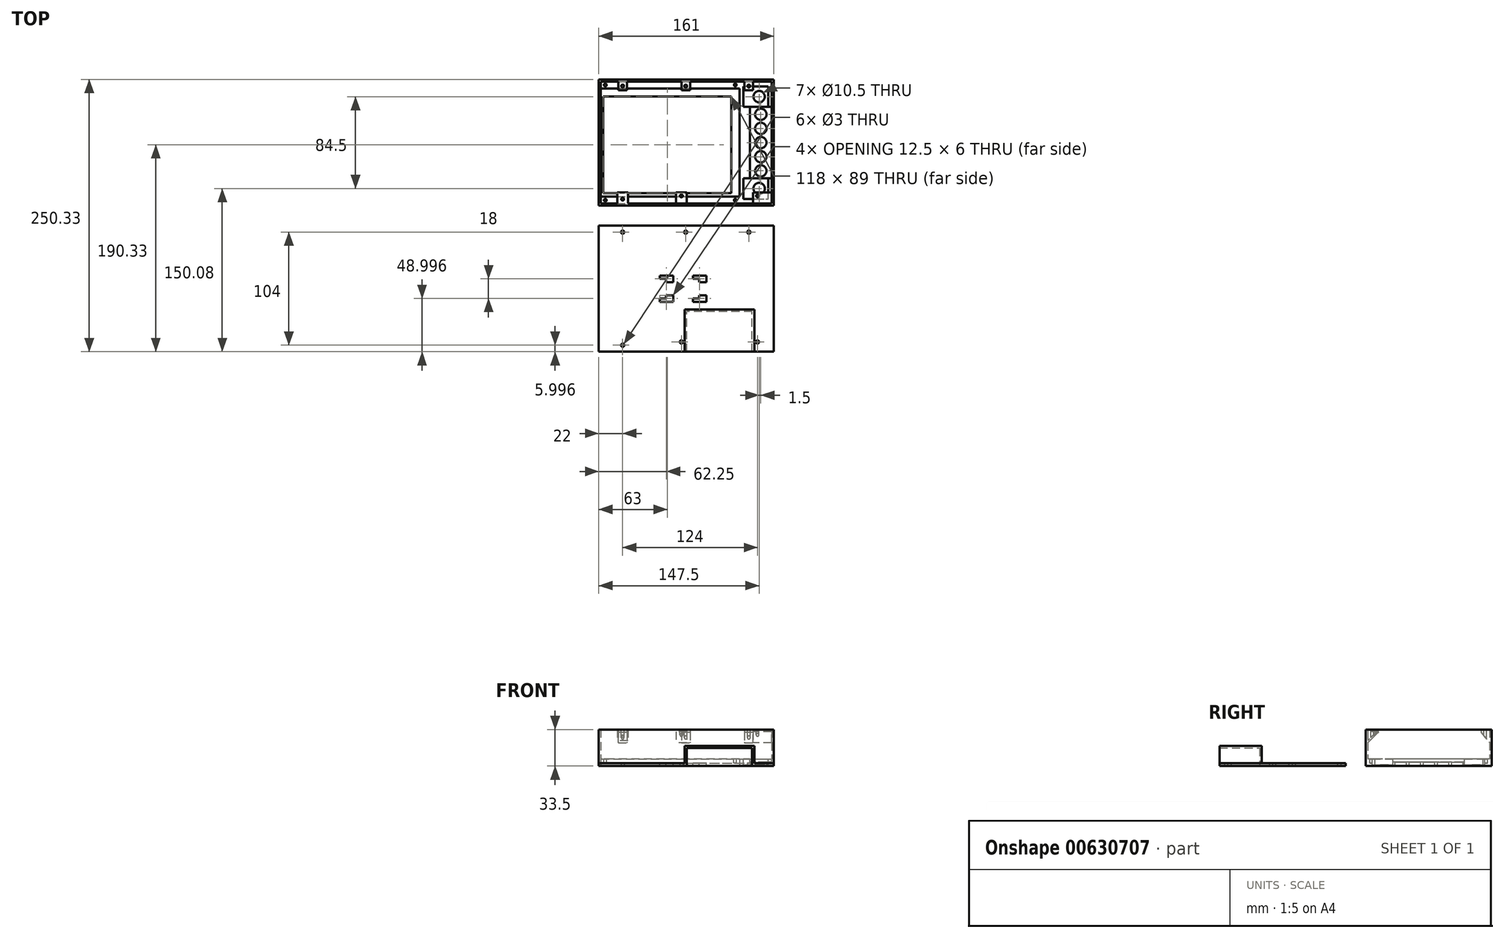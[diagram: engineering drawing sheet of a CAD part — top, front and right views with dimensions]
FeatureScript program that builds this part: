
annotation { "Feature Type Name" : "Feature", "Feature Type Description" : "" }
export const myFeature = defineFeature(function(context is Context, id is Id, definition is map)
    precondition{}
    {
        {
            var Q0;
            Q0=qCreatedBy(makeId("Top.planeOp"),FACE);
            var sketch = newSketch(context, id + "F0", { "sketchPlane" : qUnion([Q0])});
            skLineSegment(sketch, "E0.bottom", {"start": v(58, -44.5) * mm, "end": v(-60, -44.5) * mm});
            skLineSegment(sketch, "E0.top", {"start": v(58, 44.5) * mm, "end": v(-60, 44.5) * mm});
            skLineSegment(sketch, "E0.left", {"start": v(58, -44.5) * mm, "end": v(58, 44.5) * mm});
            skLineSegment(sketch, "E0.right", {"start": v(-60, -44.5) * mm, "end": v(-60, 44.5) * mm});
            skPoint(sketch, "E0.middle", {"position": v(0, 0) * mm});
            skLineSegment(sketch, "E1", {"start": v(65.5, 51.75) * mm, "end": v(-62, 51.75) * mm});
            skLineSegment(sketch, "E2", {"start": v(-62, 51.75) * mm, "end": v(-62, -47.75) * mm});
            skLineSegment(sketch, "E3", {"start": v(-62, -47.75) * mm, "end": v(65.5, -47.75) * mm});
            skLineSegment(sketch, "E4", {"start": v(97, 60) * mm, "end": v(97, -56) * mm});
            skLineSegment(sketch, "E5", {"start": v(65.5, 51.75) * mm, "end": v(65.5, -47.75) * mm});
            skLineSegment(sketch, "E6", {"start": v(97, 60) * mm, "end": v(-64, 60) * mm});
            skLineSegment(sketch, "E7", {"start": v(-64, 60) * mm, "end": v(-64, -56) * mm});
            skLineSegment(sketch, "E8", {"start": v(-64, -56) * mm, "end": v(97, -56) * mm});
            skLineSegment(sketch, "E9", {"start": v(-113.4, 0) * mm, "end": v(104.3, 0) * mm, "construction": true});
            skLineSegment(sketch, "E10", {"start": v(0, 75.63) * mm, "end": v(0, -66.3) * mm, "construction": true});
            skSolve(sketch);
        }
        {
            var Q0;
            Q0=makeQuery(id+"F0.imprint","IMPRINT",FACE,{"disambiguationData":[TD([[makeQuery(id+"F0.imprint","IMPRINT",EDGE,{"derivedFrom":sQuery(id+"F0.wireOp",EDGE,"E1")}),-1.0]])]});
            var sketch = newSketch(context, id + "F1", { "sketchPlane" : qUnion([Q0])});
            skLineSegment(sketch, "E11", {"start": v(-84.5, 2) * mm, "end": v(108.61, 2) * mm, "construction": true});
            skCircle(sketch, "E12", {"center": v(83.5, -40.25) * mm, "radius": 5.25 * mm});
            skCircle(sketch, "E13", {"center": v(83.5, 44.25) * mm, "radius": 5.25 * mm});
            skCircle(sketch, "E14", {"center": v(85, -24) * mm, "radius": 5.25 * mm});
            skCircle(sketch, "E15", {"center": v(85, -11) * mm, "radius": 5.25 * mm});
            skCircle(sketch, "E16", {"center": v(85, 2) * mm, "radius": 5.25 * mm});
            skCircle(sketch, "E17", {"center": v(85, 15) * mm, "radius": 5.25 * mm});
            skCircle(sketch, "E18", {"center": v(85, 28) * mm, "radius": 5.25 * mm});
            skLineSegment(sketch, "E19", {"start": v(83.5, -71.08) * mm, "end": v(83.5, 74.69) * mm, "construction": true});
            skLineSegment(sketch, "E20", {"start": v(85, -66.88) * mm, "end": v(85, 79.26) * mm, "construction": true});
            skLineSegment(sketch, "E21.0", {"start": v(97, 60) * mm, "end": v(-64, 60) * mm});
            skLineSegment(sketch, "E22.0", {"start": v(-64, -56) * mm, "end": v(97, -56) * mm});
            skSolve(sketch);
        }
        {
            var Q0;
            Q0=makeQuery(id+"F0.imprint","IMPRINT",FACE,{"disambiguationData":[TD([[makeQuery(id+"F0.imprint","IMPRINT",EDGE,{"derivedFrom":sQuery(id+"F0.wireOp",EDGE,"E1")}),-1.0]])]});
            extrude(context, id + "F2", {"entities" : qUnion([Q0]), "depth" : 6.5 * mm, "offsetDistance" : 25 * mm});
        }
        {
            var Q0;
            Q0=makeQuery(id+"F0.imprint","IMPRINT",FACE,{"disambiguationData":[TD([[makeQuery(id+"F0.imprint","IMPRINT",EDGE,{"derivedFrom":sQuery(id+"F0.wireOp",EDGE,"E0.bottom")}),1.0]])]});
            extrude(context, id + "F3", {"entities" : qUnion([Q0]), "operationType" : NewBodyOperationType.ADD, "depth" : 0.5 * mm, "offsetDistance" : 25 * mm});
        }
        {
            var Q0;
            Q0=qSketchRegion(id+"F1",true);
            extrude(context, id + "F4", {"entities" : qUnion([Q0]), "operationType" : NewBodyOperationType.REMOVE, "endBound" : BoundingType.UP_TO_NEXT, "depth" : 25 * mm, "offsetDistance" : 25 * mm});
        }
        {
            var Q0;
            Q0=makeQuery(id+"F2.opExtrude","CAP_FACE",FACE,{"disambiguationData":[OSD([sQuery(id+"F0.wireOp",EDGE,"E1"),sQuery(id+"F0.wireOp",EDGE,"E2"),sQuery(id+"F0.wireOp",EDGE,"E3"),sQuery(id+"F0.wireOp",EDGE,"uJP7YDUN-rWva-qcYO-6x3W-ZzMSHt70PE38"),sQuery(id+"F0.wireOp",EDGE,"E4"),sQuery(id+"F0.wireOp",EDGE,"uUVwlqNG-qbxU-A1Om-LvLD-7nAPouQdWURQ"),sQuery(id+"F0.wireOp",EDGE,"E5"),sQuery(id+"F0.wireOp",EDGE,"4ictx77T-zoG0-GI4i-ma4k-AJqkk2AVgenD"),sQuery(id+"F0.wireOp",EDGE,"E6"),sQuery(id+"F0.wireOp",EDGE,"E7"),sQuery(id+"F0.wireOp",EDGE,"E8"),sQuery(id+"F0.wireOp",EDGE,"cszChe2j-AEUY-pRS6-OkYU-3u1da41BygmN")])],"isStart":false});
            var sketch = newSketch(context, id + "F5", { "sketchPlane" : qUnion([Q0])});
            skLineSegment(sketch, "E23.bottom", {"start": v(92, 34.75) * mm, "end": v(75, 34.75) * mm});
            skLineSegment(sketch, "E23.top", {"start": v(92, 53.75) * mm, "end": v(75, 53.75) * mm});
            skLineSegment(sketch, "E23.left", {"start": v(92, 34.75) * mm, "end": v(92, 53.75) * mm});
            skLineSegment(sketch, "E23.right", {"start": v(75, 34.75) * mm, "end": v(75, 53.75) * mm});
            skPoint(sketch, "E23.middle", {"position": v(83.5, 44.25) * mm});
            skLineSegment(sketch, "E24", {"start": v(75, 53.75) * mm, "end": v(69, 53.75) * mm});
            skLineSegment(sketch, "E25", {"start": v(69, 53.75) * mm, "end": v(69, 34.75) * mm});
            skLineSegment(sketch, "E26", {"start": v(69, 34.75) * mm, "end": v(75, 34.75) * mm});
            skLineSegment(sketch, "E27.bottom", {"start": v(92, -49.75) * mm, "end": v(75, -49.75) * mm});
            skLineSegment(sketch, "E27.top", {"start": v(92, -30.75) * mm, "end": v(75, -30.75) * mm});
            skLineSegment(sketch, "E27.left", {"start": v(92, -49.75) * mm, "end": v(92, -30.75) * mm});
            skLineSegment(sketch, "E27.right", {"start": v(75, -49.75) * mm, "end": v(75, -30.75) * mm});
            skPoint(sketch, "E27.middle", {"position": v(83.5, -40.25) * mm});
            skLineSegment(sketch, "E28", {"start": v(75, -30.75) * mm, "end": v(69, -30.75) * mm});
            skLineSegment(sketch, "E29", {"start": v(69, -30.75) * mm, "end": v(69, -49.75) * mm});
            skLineSegment(sketch, "E30", {"start": v(69, -49.75) * mm, "end": v(75, -49.75) * mm});
            skLineSegment(sketch, "E31", {"start": v(75, 34.75) * mm, "end": v(75, -30.75) * mm});
            skLineSegment(sketch, "E32", {"start": v(92, 34.75) * mm, "end": v(95, 34.75) * mm});
            skLineSegment(sketch, "E33", {"start": v(95, 34.75) * mm, "end": v(95, -30.75) * mm});
            skLineSegment(sketch, "E34", {"start": v(95, -30.75) * mm, "end": v(92, -30.75) * mm});
            skSolve(sketch);
        }
        {
            var Q0;
            Q0=makeQuery(id+"F5.imprint","IMPRINT",FACE,{"disambiguationData":[TD([[makeQuery(id+"F5.imprint","IMPRINT",EDGE,{"derivedFrom":sQuery(id+"F5.wireOp",EDGE,"E23.right")}),1.0]])]});
            var Q1;
            Q1=makeQuery(id+"F5.imprint","IMPRINT",FACE,{"disambiguationData":[TD([[makeQuery(id+"F5.imprint","IMPRINT",EDGE,{"derivedFrom":sQuery(id+"F5.wireOp",EDGE,"E23.bottom")}),-1.0]])]});
            var Q2;
            Q2=makeQuery(id+"F5.imprint","IMPRINT",FACE,{"disambiguationData":[TD([[makeQuery(id+"F5.imprint","IMPRINT",EDGE,{"derivedFrom":sQuery(id+"F5.wireOp",EDGE,"E27.right")}),1.0]])]});
            var Q3;
            Q3=makeQuery(id+"F5.imprint","IMPRINT",FACE,{"disambiguationData":[TD([[makeQuery(id+"F5.imprint","IMPRINT",EDGE,{"derivedFrom":sQuery(id+"F5.wireOp",EDGE,"E27.bottom")}),-1.0]])]});
            extrude(context, id + "F6", {"entities" : qUnion([Q0, Q1, Q2, Q3]), "operationType" : NewBodyOperationType.REMOVE, "oppositeDirection" : true, "depth" : 5.5 * mm, "offsetDistance" : 25 * mm});
        }
        {
            var Q0;
            Q0=makeQuery(id+"F2.opExtrude","CAP_FACE",FACE,{"disambiguationData":[OSD([sQuery(id+"F0.wireOp",EDGE,"E1"),sQuery(id+"F0.wireOp",EDGE,"E2"),sQuery(id+"F0.wireOp",EDGE,"E3"),sQuery(id+"F0.wireOp",EDGE,"E4"),sQuery(id+"F0.wireOp",EDGE,"E5"),sQuery(id+"F0.wireOp",EDGE,"E6"),sQuery(id+"F0.wireOp",EDGE,"E7"),sQuery(id+"F0.wireOp",EDGE,"E8")])],"isStart":false});
            var sketch = newSketch(context, id + "F7", { "sketchPlane" : qUnion([Q0])});
            skLineSegment(sketch, "E35.bottom", {"start": v(-62, 58) * mm, "end": v(95, 58) * mm});
            skLineSegment(sketch, "E35.top", {"start": v(-62, -54) * mm, "end": v(95, -54) * mm});
            skLineSegment(sketch, "E35.left", {"start": v(-62, 58) * mm, "end": v(-62, -54) * mm});
            skLineSegment(sketch, "E35.right", {"start": v(95, 58) * mm, "end": v(95, -54) * mm});
            skSolve(sketch);
        }
        {
            var Q0;
            {var subQ2=sQuery(id+"F7.wireOp",EDGE,"E35.bottom");Q0=makeQuery(id+"F7.imprint","IMPRINT",FACE,{"disambiguationData":[TD([[makeQuery(id+"F7.imprint","IMPRINT",EDGE,{"derivedFrom":subQ2}),1.0]])]});}
            extrude(context, id + "F8", {"entities" : qUnion([Q0]), "operationType" : NewBodyOperationType.ADD, "depth" : 27 * mm, "offsetDistance" : 25 * mm});
        }
        {
            var Q0;
            Q0=makeQuery(id+"F2.opExtrude","CAP_FACE",FACE,{"disambiguationData":[OSD([sQuery(id+"F0.wireOp",EDGE,"E1"),sQuery(id+"F0.wireOp",EDGE,"E2"),sQuery(id+"F0.wireOp",EDGE,"E3"),sQuery(id+"F0.wireOp",EDGE,"E4"),sQuery(id+"F0.wireOp",EDGE,"E5"),sQuery(id+"F0.wireOp",EDGE,"E6"),sQuery(id+"F0.wireOp",EDGE,"E7"),sQuery(id+"F0.wireOp",EDGE,"E8")])],"isStart":false});
            var sketch = newSketch(context, id + "F9", { "sketchPlane" : qUnion([Q0])});
            skCircle(sketch, "E36", {"center": v(-58, 55) * mm, "radius": 1.25 * mm});
            skCircle(sketch, "E37", {"center": v(61.5, 55) * mm, "radius": 1.25 * mm});
            skCircle(sketch, "E38", {"center": v(61.5, -51) * mm, "radius": 1.25 * mm});
            skCircle(sketch, "E39", {"center": v(-58, -51) * mm, "radius": 1.25 * mm});
            skLineSegment(sketch, "E40", {"start": v(-58, 67) * mm, "end": v(-58, -65.08) * mm, "construction": true});
            skLineSegment(sketch, "E41", {"start": v(61.5, -67.24) * mm, "end": v(61.5, 67.67) * mm, "construction": true});
            skLineSegment(sketch, "E42", {"start": v(-91.1, 55) * mm, "end": v(105.33, 55) * mm, "construction": true});
            skLineSegment(sketch, "E43", {"start": v(-89.47, -51) * mm, "end": v(106.68, -51) * mm, "construction": true});
            skSolve(sketch);
        }
        {
            var Q0;
            Q0=makeQuery(id+"F9.imprint","IMPRINT",FACE,{"disambiguationData":[TD([[makeQuery(id+"F9.imprint","IMPRINT",EDGE,{"derivedFrom":sQuery(id+"F9.wireOp",EDGE,"E36")}),1.0]])]});
            var Q1;
            Q1=makeQuery(id+"F9.imprint","IMPRINT",FACE,{"disambiguationData":[TD([[makeQuery(id+"F9.imprint","IMPRINT",EDGE,{"derivedFrom":sQuery(id+"F9.wireOp",EDGE,"E37")}),1.0]])]});
            var Q2;
            Q2=makeQuery(id+"F9.imprint","IMPRINT",FACE,{"disambiguationData":[TD([[makeQuery(id+"F9.imprint","IMPRINT",EDGE,{"derivedFrom":sQuery(id+"F9.wireOp",EDGE,"E38")}),1.0]])]});
            var Q3;
            Q3=makeQuery(id+"F9.imprint","IMPRINT",FACE,{"disambiguationData":[TD([[makeQuery(id+"F9.imprint","IMPRINT",EDGE,{"derivedFrom":sQuery(id+"F9.wireOp",EDGE,"E39")}),1.0]])]});
            extrude(context, id + "F10", {"entities" : qUnion([Q0, Q1, Q2, Q3]), "operationType" : NewBodyOperationType.REMOVE, "oppositeDirection" : true, "depth" : 4 * mm, "offsetDistance" : 25 * mm});
        }
        {
            var Q0;
            Q0=makeQuery(id+"F8.opExtrude","SWEPT_FACE",FACE,{"disambiguationData":[OSD([sQuery(id+"F7.wireOp",EDGE,"E35.bottom")])]});
            var sketch = newSketch(context, id + "F11", { "sketchPlane" : qUnion([Q0])});
            skLineSegment(sketch, "E44.bottom", {"start": v(-46, 33.5) * mm, "end": v(-38, 33.5) * mm});
            skLineSegment(sketch, "E44.top", {"start": v(-46, 21.5) * mm, "end": v(-38, 21.5) * mm});
            skLineSegment(sketch, "E44.left", {"start": v(-46, 33.5) * mm, "end": v(-46, 21.5) * mm});
            skLineSegment(sketch, "E44.right", {"start": v(-38, 33.5) * mm, "end": v(-38, 21.5) * mm});
            skLineSegment(sketch, "E45.bottom", {"start": v(12, 33.5) * mm, "end": v(20, 33.5) * mm});
            skLineSegment(sketch, "E45.top", {"start": v(12, 21.5) * mm, "end": v(20, 21.5) * mm});
            skLineSegment(sketch, "E45.left", {"start": v(12, 33.5) * mm, "end": v(12, 21.5) * mm});
            skLineSegment(sketch, "E45.right", {"start": v(20, 33.5) * mm, "end": v(20, 21.5) * mm});
            skLineSegment(sketch, "E46.bottom", {"start": v(70, 33.5) * mm, "end": v(78, 33.5) * mm});
            skLineSegment(sketch, "E46.top", {"start": v(70, 21.5) * mm, "end": v(78, 21.5) * mm});
            skLineSegment(sketch, "E46.left", {"start": v(70, 33.5) * mm, "end": v(70, 21.5) * mm});
            skLineSegment(sketch, "E46.right", {"start": v(78, 33.5) * mm, "end": v(78, 21.5) * mm});
            skSolve(sketch);
        }
        {
            var Q0;
            Q0=makeQuery(id+"F11.imprint","IMPRINT",FACE,{"disambiguationData":[TD([[makeQuery(id+"F11.imprint","IMPRINT",EDGE,{"derivedFrom":sQuery(id+"F11.wireOp",EDGE,"E44.bottom")}),-1.0]])]});
            var Q1;
            Q1=makeQuery(id+"F11.imprint","IMPRINT",FACE,{"disambiguationData":[TD([[makeQuery(id+"F11.imprint","IMPRINT",EDGE,{"derivedFrom":sQuery(id+"F11.wireOp",EDGE,"E45.bottom")}),-1.0]])]});
            var Q2;
            Q2=makeQuery(id+"F11.imprint","IMPRINT",FACE,{"disambiguationData":[TD([[makeQuery(id+"F11.imprint","IMPRINT",EDGE,{"derivedFrom":sQuery(id+"F11.wireOp",EDGE,"E46.bottom")}),-1.0]])]});
            extrude(context, id + "F12", {"entities" : qUnion([Q0, Q1, Q2]), "operationType" : NewBodyOperationType.ADD, "depth" : 8 * mm, "offsetDistance" : 25 * mm});
        }
        {
            var Q0;
            Q0=makeQuery(id+"F12.opExtrude","SWEPT_FACE",FACE,{"disambiguationData":[OSD([sQuery(id+"F11.wireOp",EDGE,"E44.left")])]});
            var sketch = newSketch(context, id + "F13", { "sketchPlane" : qUnion([Q0])});
            skLineSegment(sketch, "E47", {"start": v(-58, 21.5) * mm, "end": v(-50, 31.03) * mm});
            skSolve(sketch);
        }
        {
            var Q0;
            {var subQ0=sQuery(id+"F13.wireOp",EDGE,"E47");Q0=makeQuery(id+"F13.imprint","IMPRINT",FACE,{"disambiguationData":[TD([[makeQuery(id+"F13.imprint","IMPRINT",EDGE,{"derivedFrom":subQ0}),-1.0]])]});}
            var Q1;
            Q1=makeQuery(id+"F12.opExtrude","SWEPT_FACE",FACE,{"disambiguationData":[OSD([sQuery(id+"F11.wireOp",EDGE,"E46.right")])]});
            extrude(context, id + "F14", {"entities" : qUnion([Q0]), "operationType" : NewBodyOperationType.REMOVE, "endBound" : BoundingType.UP_TO_SURFACE, "oppositeDirection" : true, "depth" : 25 * mm, "endBoundEntityFace" : qUnion([Q1]), "offsetDistance" : 25 * mm});
        }
        {
            var Q0;
            Q0=makeQuery(id+"F8.opExtrude","SWEPT_FACE",FACE,{"disambiguationData":[OSD([sQuery(id+"F7.wireOp",EDGE,"E35.top")])]});
            var sketch = newSketch(context, id + "F15", { "sketchPlane" : qUnion([Q0])});
            skLineSegment(sketch, "E48.bottom", {"start": v(-95, 31.7) * mm, "end": v(-78, 31.7) * mm});
            skLineSegment(sketch, "E48.top", {"start": v(-95, 21.5) * mm, "end": v(-78, 21.5) * mm});
            skLineSegment(sketch, "E48.left", {"start": v(-95, 31.7) * mm, "end": v(-95, 21.5) * mm});
            skLineSegment(sketch, "E48.right", {"start": v(-78, 31.7) * mm, "end": v(-78, 21.5) * mm});
            skLineSegment(sketch, "E49.bottom", {"start": v(-17, 31.7) * mm, "end": v(-7, 31.7) * mm});
            skLineSegment(sketch, "E49.top", {"start": v(-17, 21.5) * mm, "end": v(-7, 21.5) * mm});
            skLineSegment(sketch, "E49.left", {"start": v(-17, 31.7) * mm, "end": v(-17, 21.5) * mm});
            skLineSegment(sketch, "E49.right", {"start": v(-7, 31.7) * mm, "end": v(-7, 21.5) * mm});
            skLineSegment(sketch, "E50.bottom", {"start": v(37, 33.5) * mm, "end": v(47, 33.5) * mm});
            skLineSegment(sketch, "E50.top", {"start": v(37, 23.3) * mm, "end": v(47, 23.3) * mm});
            skLineSegment(sketch, "E50.left", {"start": v(37, 33.5) * mm, "end": v(37, 23.3) * mm});
            skLineSegment(sketch, "E50.right", {"start": v(47, 33.5) * mm, "end": v(47, 23.3) * mm});
            skLineSegment(sketch, "E51.0", {"start": v(-95, 33.5) * mm, "end": v(-95, 6.5) * mm});
            skLineSegment(sketch, "E52.0", {"start": v(62, 33.5) * mm, "end": v(62, 6.5) * mm});
            skSolve(sketch);
        }
        {
            var Q0;
            Q0=makeQuery(id+"F15.imprint","IMPRINT",FACE,{"disambiguationData":[TD([[makeQuery(id+"F15.imprint","IMPRINT",EDGE,{"derivedFrom":sQuery(id+"F15.wireOp",EDGE,"E50.bottom")}),1.0]])]});
            var Q1;
            Q1=makeQuery(id+"F15.imprint","IMPRINT",FACE,{"disambiguationData":[TD([[makeQuery(id+"F15.imprint","IMPRINT",EDGE,{"derivedFrom":sQuery(id+"F15.wireOp",EDGE,"E49.bottom")}),-1.0]])]});
            var Q2;
            {var subQ0=sQuery(id+"F15.wireOp",EDGE,"E48.bottom");Q2=makeQuery(id+"F15.imprint","IMPRINT",FACE,{"disambiguationData":[TD([[makeQuery(id+"F15.imprint","IMPRINT",EDGE,{"derivedFrom":subQ0}),-1.0]])]});}
            extrude(context, id + "F16", {"entities" : qUnion([Q0, Q1, Q2]), "operationType" : NewBodyOperationType.ADD, "depth" : 10 * mm, "offsetDistance" : 25 * mm});
        }
        {
            var Q0;
            Q0=makeQuery(id+"F16.opExtrude","SWEPT_FACE",FACE,{"disambiguationData":[OSD([sQuery(id+"F15.wireOp",EDGE,"E49.right")])]});
            var sketch = newSketch(context, id + "F17", { "sketchPlane" : qUnion([Q0])});
            skLineSegment(sketch, "E53", {"start": v(54, 21.5) * mm, "end": v(44, 31.7) * mm});
            skSolve(sketch);
        }
        {
            var Q0;
            Q0=makeQuery(id+"F17.imprint","IMPRINT",FACE,{"disambiguationData":[TD([[makeQuery(id+"F17.imprint","IMPRINT",EDGE,{"derivedFrom":sQuery(id+"F17.wireOp",EDGE,"E53")}),1.0]])]});
            var Q1;
            Q1=makeQuery(id+"F8.opExtrude","SWEPT_FACE",FACE,{"disambiguationData":[OSD([sQuery(id+"F7.wireOp",EDGE,"E35.right")])]});
            extrude(context, id + "F18", {"entities" : qUnion([Q0]), "operationType" : NewBodyOperationType.REMOVE, "endBound" : BoundingType.UP_TO_SURFACE, "oppositeDirection" : true, "depth" : 25 * mm, "endBoundEntityFace" : qUnion([Q1]), "offsetDistance" : 25 * mm});
        }
        {
            var Q0;
            Q0=makeQuery(id+"F16.boolean.opBoolean","MERGE",FACE,{"derivedFrom":[makeQuery(id+"F12.boolean.opBoolean","MERGE",FACE,{"derivedFrom":[makeQuery(id+"F8.opExtrude","CAP_FACE",FACE,{"disambiguationData":[OSD([sQuery(id+"F0.wireOp",EDGE,"E4"),sQuery(id+"F0.wireOp",EDGE,"E6"),sQuery(id+"F0.wireOp",EDGE,"E7"),sQuery(id+"F0.wireOp",EDGE,"E8"),sQuery(id+"F7.wireOp",EDGE,"E35.bottom"),sQuery(id+"F7.wireOp",EDGE,"E35.top"),sQuery(id+"F7.wireOp",EDGE,"E35.left"),sQuery(id+"F7.wireOp",EDGE,"E35.right")])],"isStart":false}),makeQuery(id+"F12.opExtrude","SWEPT_FACE",FACE,{"disambiguationData":[OSD([sQuery(id+"F11.wireOp",EDGE,"E44.bottom")])]}),makeQuery(id+"F12.opExtrude","SWEPT_FACE",FACE,{"disambiguationData":[OSD([sQuery(id+"F11.wireOp",EDGE,"E45.bottom")])]}),makeQuery(id+"F12.opExtrude","SWEPT_FACE",FACE,{"disambiguationData":[OSD([sQuery(id+"F11.wireOp",EDGE,"E46.bottom")])]})]}),makeQuery(id+"F16.opExtrude","SWEPT_FACE",FACE,{"disambiguationData":[OSD([sQuery(id+"F15.wireOp",EDGE,"E48.bottom")])]}),makeQuery(id+"F16.opExtrude","SWEPT_FACE",FACE,{"disambiguationData":[OSD([sQuery(id+"F15.wireOp",EDGE,"E49.bottom")])]}),makeQuery(id+"F16.opExtrude","SWEPT_FACE",FACE,{"disambiguationData":[OSD([sQuery(id+"F15.wireOp",EDGE,"E50.bottom")])]})]});
            var sketch = newSketch(context, id + "F19", { "sketchPlane" : qUnion([Q0])});
            skCircle(sketch, "E54", {"center": v(-42, 54) * mm, "radius": 1.3 * mm});
            skCircle(sketch, "E55", {"center": v(16, 54) * mm, "radius": 1.3 * mm});
            skCircle(sketch, "E56", {"center": v(74, 54) * mm, "radius": 1.3 * mm});
            skCircle(sketch, "E57", {"center": v(-42, -50) * mm, "radius": 1.3 * mm});
            skCircle(sketch, "E58", {"center": v(12, -47) * mm, "radius": 1.3 * mm});
            skCircle(sketch, "E59", {"center": v(82, -47) * mm, "radius": 1.3 * mm});
            skSolve(sketch);
        }
        {
            var Q0;
            Q0=makeQuery(id+"F19.imprint","IMPRINT",FACE,{"disambiguationData":[TD([[makeQuery(id+"F19.imprint","IMPRINT",EDGE,{"derivedFrom":sQuery(id+"F19.wireOp",EDGE,"E56")}),1.0]])]});
            var Q1;
            Q1=makeQuery(id+"F19.imprint","IMPRINT",FACE,{"disambiguationData":[TD([[makeQuery(id+"F19.imprint","IMPRINT",EDGE,{"derivedFrom":sQuery(id+"F19.wireOp",EDGE,"E57")}),1.0]])]});
            var Q2;
            Q2=makeQuery(id+"F19.imprint","IMPRINT",FACE,{"disambiguationData":[TD([[makeQuery(id+"F19.imprint","IMPRINT",EDGE,{"derivedFrom":sQuery(id+"F19.wireOp",EDGE,"E58")}),1.0]])]});
            var Q3;
            Q3=makeQuery(id+"F19.imprint","IMPRINT",FACE,{"disambiguationData":[TD([[makeQuery(id+"F19.imprint","IMPRINT",EDGE,{"derivedFrom":sQuery(id+"F19.wireOp",EDGE,"E59")}),1.0]])]});
            var Q4;
            Q4=makeQuery(id+"F19.imprint","IMPRINT",FACE,{"disambiguationData":[TD([[makeQuery(id+"F19.imprint","IMPRINT",EDGE,{"derivedFrom":sQuery(id+"F19.wireOp",EDGE,"E54")}),1.0]])]});
            var Q5;
            Q5=makeQuery(id+"F19.imprint","IMPRINT",FACE,{"disambiguationData":[TD([[makeQuery(id+"F19.imprint","IMPRINT",EDGE,{"derivedFrom":sQuery(id+"F19.wireOp",EDGE,"E55")}),1.0]])]});
            var Q6;
            Q6=makeQuery(id+"F2.opExtrude","CAP_FACE",FACE,{"disambiguationData":[OSD([sQuery(id+"F0.wireOp",EDGE,"E1"),sQuery(id+"F0.wireOp",EDGE,"E2"),sQuery(id+"F0.wireOp",EDGE,"E3"),sQuery(id+"F0.wireOp",EDGE,"E4"),sQuery(id+"F0.wireOp",EDGE,"E5"),sQuery(id+"F0.wireOp",EDGE,"E6"),sQuery(id+"F0.wireOp",EDGE,"E7"),sQuery(id+"F0.wireOp",EDGE,"E8")])],"isStart":false});
            extrude(context, id + "F20", {"entities" : qUnion([Q0, Q1, Q2, Q3, Q4, Q5]), "operationType" : NewBodyOperationType.REMOVE, "endBound" : BoundingType.UP_TO_SURFACE, "oppositeDirection" : true, "depth" : 25 * mm, "endBoundEntityFace" : qUnion([Q6]), "offsetDistance" : 25 * mm});
        }
        {
            var Q0;
            Q0=makeQuery(id+"F5.imprint","IMPRINT",FACE,{"disambiguationData":[TD([[makeQuery(id+"F5.imprint","IMPRINT",EDGE,{"derivedFrom":sQuery(id+"F5.wireOp",EDGE,"E23.bottom")}),1.0]])]});
            extrude(context, id + "F21", {"entities" : qUnion([Q0]), "operationType" : NewBodyOperationType.REMOVE, "oppositeDirection" : true, "depth" : 3 * mm, "offsetDistance" : 25 * mm});
        }
        {
            var Q0;
            Q0=qCreatedBy(makeId("Top.planeOp"),FACE);
            var sketch = newSketch(context, id + "F22", { "sketchPlane" : qUnion([Q0])});
            skLineSegment(sketch, "E60.bottom", {"start": v(-64, -74.33) * mm, "end": v(97, -74.33) * mm});
            skLineSegment(sketch, "E60.top", {"start": v(-64, -190.33) * mm, "end": v(97, -190.33) * mm});
            skLineSegment(sketch, "E60.left", {"start": v(-64, -74.33) * mm, "end": v(-64, -190.33) * mm});
            skLineSegment(sketch, "E60.right", {"start": v(97, -74.33) * mm, "end": v(97, -190.33) * mm});
            skLineSegment(sketch, "E61", {"start": v(-105.96, -80.33) * mm, "end": v(122.08, -80.33) * mm, "construction": true});
            skLineSegment(sketch, "E62", {"start": v(-105.44, -184.33) * mm, "end": v(113.73, -184.33) * mm, "construction": true});
            skLineSegment(sketch, "E63", {"start": v(-42, -64.7) * mm, "end": v(-42, -93.96) * mm, "construction": true});
            skLineSegment(sketch, "E64", {"start": v(16, -65.92) * mm, "end": v(16, -94.49) * mm, "construction": true});
            skLineSegment(sketch, "E65", {"start": v(74, -64.42) * mm, "end": v(74, -94.86) * mm, "construction": true});
            skCircle(sketch, "E66", {"center": v(-42, -80.33) * mm, "radius": 1.5 * mm});
            skCircle(sketch, "E67", {"center": v(16, -80.33) * mm, "radius": 1.5 * mm});
            skCircle(sketch, "E68", {"center": v(74, -80.33) * mm, "radius": 1.5 * mm});
            skCircle(sketch, "E69", {"center": v(82, -181.33) * mm, "radius": 1.5 * mm});
            skCircle(sketch, "E70", {"center": v(12, -181.33) * mm, "radius": 1.5 * mm});
            skCircle(sketch, "E71", {"center": v(-42, -184.33) * mm, "radius": 1.5 * mm});
            skPoint(sketch, "E72.0", {"position": v(-42, -50) * mm});
            skPoint(sketch, "E73.0", {"position": v(12, -47) * mm});
            skLineSegment(sketch, "E74", {"start": v(-42, -50) * mm, "end": v(-42, -209.96) * mm, "construction": true});
            skLineSegment(sketch, "E75", {"start": v(12, -47) * mm, "end": v(12, -206.82) * mm, "construction": true});
            skPoint(sketch, "E75.endSnap0", {"position": v(12, -80.14) * mm});
            skPoint(sketch, "E76.0", {"position": v(82, -47) * mm});
            skLineSegment(sketch, "E77", {"start": v(82, -167.56) * mm, "end": v(82, -211.76) * mm, "construction": true});
            skLineSegment(sketch, "E78", {"start": v(47, -161.86) * mm, "end": v(47, -205.17) * mm, "construction": true});
            skLineSegment(sketch, "E79.bottom", {"start": v(77, -190.33) * mm, "end": v(17, -190.33) * mm});
            skLineSegment(sketch, "E79.top", {"start": v(77, -153.33) * mm, "end": v(17, -153.33) * mm});
            skLineSegment(sketch, "E79.left", {"start": v(77, -190.33) * mm, "end": v(77, -153.33) * mm});
            skLineSegment(sketch, "E79.right", {"start": v(17, -190.33) * mm, "end": v(17, -153.33) * mm});
            skPoint(sketch, "E79.middle", {"position": v(47, -171.83) * mm});
            skSolve(sketch);
        }
        {
            var Q0;
            Q0=makeQuery(id+"F22.imprint","IMPRINT",FACE,{"disambiguationData":[TD([[makeQuery(id+"F22.imprint","IMPRINT",EDGE,{"derivedFrom":sQuery(id+"F22.wireOp",EDGE,"E60.bottom")}),-1.0]])]});
            extrude(context, id + "F23", {"entities" : qUnion([Q0]), "depth" : 2.5 * mm, "offsetDistance" : 25 * mm});
        }
        {
            var Q0;
            Q0=makeQuery(id+"F23.opExtrude","CAP_FACE",FACE,{"disambiguationData":[OSD([sQuery(id+"F22.wireOp",EDGE,"E60.bottom"),sQuery(id+"F22.wireOp",EDGE,"E60.top"),sQuery(id+"F22.wireOp",EDGE,"E60.left"),sQuery(id+"F22.wireOp",EDGE,"E60.right"),sQuery(id+"F22.wireOp",EDGE,"E66"),sQuery(id+"F22.wireOp",EDGE,"E67"),sQuery(id+"F22.wireOp",EDGE,"E68"),sQuery(id+"F22.wireOp",EDGE,"E69"),sQuery(id+"F22.wireOp",EDGE,"E70"),sQuery(id+"F22.wireOp",EDGE,"E71")])],"isStart":false});
            var sketch = newSketch(context, id + "F24", { "sketchPlane" : qUnion([Q0])});
            skLineSegment(sketch, "E80.bottom", {"start": v(31.75, -141.33) * mm, "end": v(1.25, -141.33) * mm, "construction": true});
            skLineSegment(sketch, "E80.top", {"start": v(31.75, -123.33) * mm, "end": v(1.25, -123.33) * mm, "construction": true});
            skLineSegment(sketch, "E80.left", {"start": v(31.75, -141.33) * mm, "end": v(31.75, -123.33) * mm, "construction": true});
            skLineSegment(sketch, "E80.right", {"start": v(1.25, -141.33) * mm, "end": v(1.25, -123.33) * mm, "construction": true});
            skPoint(sketch, "E80.middle", {"position": v(16.5, -132.33) * mm});
            skLineSegment(sketch, "E81.bottom", {"start": v(4.5, -126.33) * mm, "end": v(-2, -126.33) * mm});
            skLineSegment(sketch, "E81.top", {"start": v(4.5, -120.33) * mm, "end": v(-2, -120.33) * mm});
            skLineSegment(sketch, "E81.left", {"start": v(4.5, -126.33) * mm, "end": v(4.5, -120.33) * mm});
            skLineSegment(sketch, "E81.right", {"start": v(-2, -126.33) * mm, "end": v(-2, -120.33) * mm});
            skPoint(sketch, "E81.middle", {"position": v(1.25, -123.33) * mm});
            skLineSegment(sketch, "E82.bottom", {"start": v(35, -126.33) * mm, "end": v(28.5, -126.33) * mm});
            skLineSegment(sketch, "E82.top", {"start": v(35, -120.33) * mm, "end": v(28.5, -120.33) * mm});
            skLineSegment(sketch, "E82.left", {"start": v(35, -126.33) * mm, "end": v(35, -120.33) * mm});
            skLineSegment(sketch, "E82.right", {"start": v(28.5, -126.33) * mm, "end": v(28.5, -120.33) * mm});
            skPoint(sketch, "E82.middle", {"position": v(31.75, -123.33) * mm});
            skLineSegment(sketch, "E83.bottom", {"start": v(35, -144.33) * mm, "end": v(28.5, -144.33) * mm});
            skLineSegment(sketch, "E83.top", {"start": v(35, -138.33) * mm, "end": v(28.5, -138.33) * mm});
            skLineSegment(sketch, "E83.left", {"start": v(35, -144.33) * mm, "end": v(35, -138.33) * mm});
            skLineSegment(sketch, "E83.right", {"start": v(28.5, -144.33) * mm, "end": v(28.5, -138.33) * mm});
            skPoint(sketch, "E83.middle", {"position": v(31.75, -141.33) * mm});
            skLineSegment(sketch, "E84.bottom", {"start": v(4.5, -144.33) * mm, "end": v(-2, -144.33) * mm});
            skLineSegment(sketch, "E84.top", {"start": v(4.5, -138.33) * mm, "end": v(-2, -138.33) * mm});
            skLineSegment(sketch, "E84.left", {"start": v(4.5, -144.33) * mm, "end": v(4.5, -138.33) * mm});
            skLineSegment(sketch, "E84.right", {"start": v(-2, -144.33) * mm, "end": v(-2, -138.33) * mm});
            skPoint(sketch, "E84.middle", {"position": v(1.25, -141.33) * mm});
            skLineSegment(sketch, "E85", {"start": v(-2, -123.33) * mm, "end": v(-8, -123.33) * mm});
            skLineSegment(sketch, "E86", {"start": v(-8, -123.33) * mm, "end": v(-8, -120.33) * mm});
            skLineSegment(sketch, "E87", {"start": v(-8, -120.33) * mm, "end": v(-2, -120.33) * mm});
            skLineSegment(sketch, "E88", {"start": v(-2, -141.33) * mm, "end": v(-8, -141.33) * mm});
            skLineSegment(sketch, "E89", {"start": v(-8, -141.33) * mm, "end": v(-8, -144.33) * mm});
            skLineSegment(sketch, "E90", {"start": v(-8, -144.33) * mm, "end": v(-2, -144.33) * mm});
            skLineSegment(sketch, "E91", {"start": v(28.5, -123.33) * mm, "end": v(22.5, -123.33) * mm});
            skLineSegment(sketch, "E92", {"start": v(22.5, -123.33) * mm, "end": v(22.5, -120.33) * mm});
            skLineSegment(sketch, "E93", {"start": v(22.5, -120.33) * mm, "end": v(28.5, -120.33) * mm});
            skLineSegment(sketch, "E94", {"start": v(28.5, -144.33) * mm, "end": v(22.5, -144.33) * mm});
            skLineSegment(sketch, "E95", {"start": v(22.5, -144.33) * mm, "end": v(22.5, -141.33) * mm});
            skLineSegment(sketch, "E96", {"start": v(22.5, -141.33) * mm, "end": v(28.5, -141.33) * mm});
            skSolve(sketch);
        }
        {
            var Q0;
            {var subQ2=sQuery(id+"F24.wireOp",EDGE,"E85");Q0=makeQuery(id+"F24.imprint","IMPRINT",FACE,{"disambiguationData":[TD([[makeQuery(id+"F24.imprint","IMPRINT",EDGE,{"derivedFrom":subQ2}),-1.0]])]});}
            var Q1;
            {var subQ1=sQuery(id+"F24.wireOp",EDGE,"E81.bottom");Q1=makeQuery(id+"F24.imprint","IMPRINT",FACE,{"disambiguationData":[TD([[makeQuery(id+"F24.imprint","IMPRINT",EDGE,{"derivedFrom":subQ1}),-1.0]])]});}
            var Q2;
            {var subQ2=sQuery(id+"F24.wireOp",EDGE,"E91");Q2=makeQuery(id+"F24.imprint","IMPRINT",FACE,{"disambiguationData":[TD([[makeQuery(id+"F24.imprint","IMPRINT",EDGE,{"derivedFrom":subQ2}),-1.0]])]});}
            var Q3;
            {var subQ1=sQuery(id+"F24.wireOp",EDGE,"E82.bottom");Q3=makeQuery(id+"F24.imprint","IMPRINT",FACE,{"disambiguationData":[TD([[makeQuery(id+"F24.imprint","IMPRINT",EDGE,{"derivedFrom":subQ1}),-1.0]])]});}
            var Q4;
            {var subQ1=sQuery(id+"F24.wireOp",EDGE,"E83.bottom");Q4=makeQuery(id+"F24.imprint","IMPRINT",FACE,{"disambiguationData":[TD([[makeQuery(id+"F24.imprint","IMPRINT",EDGE,{"derivedFrom":subQ1}),-1.0]])]});}
            var Q5;
            {var subQ0=sQuery(id+"F24.wireOp",EDGE,"E94");Q5=makeQuery(id+"F24.imprint","IMPRINT",FACE,{"disambiguationData":[TD([[makeQuery(id+"F24.imprint","IMPRINT",EDGE,{"derivedFrom":subQ0}),-1.0]])]});}
            var Q6;
            {var subQ1=sQuery(id+"F24.wireOp",EDGE,"E84.bottom");Q6=makeQuery(id+"F24.imprint","IMPRINT",FACE,{"disambiguationData":[TD([[makeQuery(id+"F24.imprint","IMPRINT",EDGE,{"derivedFrom":subQ1}),-1.0]])]});}
            var Q7;
            {var subQ2=sQuery(id+"F24.wireOp",EDGE,"E88");Q7=makeQuery(id+"F24.imprint","IMPRINT",FACE,{"disambiguationData":[TD([[makeQuery(id+"F24.imprint","IMPRINT",EDGE,{"derivedFrom":subQ2}),1.0]])]});}
            extrude(context, id + "F25", {"entities" : qUnion([Q0, Q1, Q2, Q3, Q4, Q5, Q6, Q7]), "operationType" : NewBodyOperationType.REMOVE, "endBound" : BoundingType.THROUGH_ALL, "oppositeDirection" : true, "depth" : 25 * mm, "offsetDistance" : 25 * mm});
        }
        {
            var Q0;
            Q0=makeQuery(id+"F19.imprint","IMPRINT",FACE,{"disambiguationData":[TD([[makeQuery(id+"F19.imprint","IMPRINT",EDGE,{"derivedFrom":sQuery(id+"F19.wireOp",EDGE,"E59")}),1.0]])]});
            var Q1;
            Q1=makeQuery(id+"F2.opExtrude","CAP_FACE",FACE,{"disambiguationData":[OSD([sQuery(id+"F0.wireOp",EDGE,"E1"),sQuery(id+"F0.wireOp",EDGE,"E2"),sQuery(id+"F0.wireOp",EDGE,"E3"),sQuery(id+"F0.wireOp",EDGE,"E4"),sQuery(id+"F0.wireOp",EDGE,"E5"),sQuery(id+"F0.wireOp",EDGE,"E6"),sQuery(id+"F0.wireOp",EDGE,"E7"),sQuery(id+"F0.wireOp",EDGE,"E8")])],"isStart":false});
            extrude(context, id + "F26", {"entities" : qUnion([Q0]), "operationType" : NewBodyOperationType.REMOVE, "endBound" : BoundingType.UP_TO_SURFACE, "oppositeDirection" : true, "depth" : 25 * mm, "endBoundEntityFace" : qUnion([Q1]), "offsetDistance" : 25 * mm});
        }
        {
            var Q0;
            Q0=makeQuery(id+"F16.opExtrude","SWEPT_FACE",FACE,{"disambiguationData":[OSD([sQuery(id+"F15.wireOp",EDGE,"E50.left")])]});
            var sketch = newSketch(context, id + "F27", { "sketchPlane" : qUnion([Q0])});
            skLineSegment(sketch, "E97", {"start": v(-54, 23.3) * mm, "end": v(-44, 33.5) * mm});
            skSolve(sketch);
        }
        {
            var Q0;
            Q0=makeQuery(id+"F27.imprint","IMPRINT",FACE,{"disambiguationData":[TD([[makeQuery(id+"F27.imprint","IMPRINT",EDGE,{"derivedFrom":sQuery(id+"F27.wireOp",EDGE,"E97")}),-1.0]])]});
            var Q1;
            Q1=makeQuery(id+"F8.boolean.opBoolean","MERGE",FACE,{"derivedFrom":[makeQuery(id+"F2.opExtrude","SWEPT_FACE",FACE,{"disambiguationData":[OSD([sQuery(id+"F0.wireOp",EDGE,"E2")])]}),makeQuery(id+"F8.opExtrude","SWEPT_FACE",FACE,{"disambiguationData":[OSD([sQuery(id+"F7.wireOp",EDGE,"E35.left")])]})]});
            extrude(context, id + "F28", {"entities" : qUnion([Q0]), "operationType" : NewBodyOperationType.REMOVE, "endBound" : BoundingType.UP_TO_SURFACE, "oppositeDirection" : true, "depth" : 25 * mm, "endBoundEntityFace" : qUnion([Q1]), "offsetDistance" : 25 * mm});
        }
        {
            var Q0;
            Q0=makeQuery(id+"F23.opExtrude","CAP_FACE",FACE,{"disambiguationData":[OSD([sQuery(id+"F22.wireOp",EDGE,"E60.bottom"),sQuery(id+"F22.wireOp",EDGE,"E60.top"),sQuery(id+"F22.wireOp",EDGE,"E60.left"),sQuery(id+"F22.wireOp",EDGE,"E60.right"),sQuery(id+"F22.wireOp",EDGE,"E66"),sQuery(id+"F22.wireOp",EDGE,"E67"),sQuery(id+"F22.wireOp",EDGE,"E68"),sQuery(id+"F22.wireOp",EDGE,"E69"),sQuery(id+"F22.wireOp",EDGE,"E70"),sQuery(id+"F22.wireOp",EDGE,"E71"),sQuery(id+"F22.wireOp",EDGE,"E79.top"),sQuery(id+"F22.wireOp",EDGE,"E79.left"),sQuery(id+"F22.wireOp",EDGE,"E79.right")])],"isStart":false});
            var sketch = newSketch(context, id + "F29", { "sketchPlane" : qUnion([Q0])});
            skLineSegment(sketch, "E98", {"start": v(15, -190.33) * mm, "end": v(15, -151.33) * mm});
            skLineSegment(sketch, "E99", {"start": v(15, -151.33) * mm, "end": v(79, -151.33) * mm});
            skLineSegment(sketch, "E100", {"start": v(79, -151.33) * mm, "end": v(79, -190.33) * mm});
            skSolve(sketch);
        }
        {
            var Q0;
            {var subQ3=sQuery(id+"F29.wireOp",EDGE,"E98");Q0=makeQuery(id+"F29.imprint","IMPRINT",FACE,{"disambiguationData":[TD([[makeQuery(id+"F29.imprint","IMPRINT",EDGE,{"derivedFrom":subQ3}),-1.0]])]});}
            extrude(context, id + "F30", {"entities" : qUnion([Q0]), "operationType" : NewBodyOperationType.ADD, "depth" : 14 * mm, "offsetDistance" : 25 * mm});
        }
        {
            var Q0;
            Q0=makeQuery(id+"F30.opExtrude","CAP_FACE",FACE,{"disambiguationData":[OSD([sQuery(id+"F22.wireOp",EDGE,"E60.top"),sQuery(id+"F22.wireOp",EDGE,"E79.top"),sQuery(id+"F22.wireOp",EDGE,"E79.left"),sQuery(id+"F22.wireOp",EDGE,"E79.right"),sQuery(id+"F29.wireOp",EDGE,"E98"),sQuery(id+"F29.wireOp",EDGE,"E99"),sQuery(id+"F29.wireOp",EDGE,"E100")])],"isStart":false});
            var sketch = newSketch(context, id + "F31", { "sketchPlane" : qUnion([Q0])});
            skLineSegment(sketch, "E101.bottom", {"start": v(79, -190.33) * mm, "end": v(15, -190.33) * mm});
            skLineSegment(sketch, "E101.top", {"start": v(79, -151.33) * mm, "end": v(15, -151.33) * mm});
            skLineSegment(sketch, "E101.left", {"start": v(79, -190.33) * mm, "end": v(79, -151.33) * mm});
            skLineSegment(sketch, "E101.right", {"start": v(15, -190.33) * mm, "end": v(15, -151.33) * mm});
            skSolve(sketch);
        }
        {
            var Q0;
            Q0=makeQuery(id+"F31.imprint","IMPRINT",FACE,{"disambiguationData":[TD([[makeQuery(id+"F31.imprint","IMPRINT",EDGE,{"derivedFrom":makeQuery(id+"F30.opExtrude","CAP_EDGE",EDGE,{"disambiguationData":[OSD([sQuery(id+"F22.wireOp",EDGE,"E79.top")])],"isStart":false})}),1.0]])]});
            var Q1;
            Q1=makeQuery(id+"F31.imprint","IMPRINT",FACE,{"disambiguationData":[TD([[makeQuery(id+"F31.imprint","IMPRINT",EDGE,{"derivedFrom":sQuery(id+"F31.wireOp",EDGE,"E101.top")}),-1.0]])]});
            extrude(context, id + "F32", {"entities" : qUnion([Q0, Q1]), "operationType" : NewBodyOperationType.ADD, "depth" : 2 * mm, "offsetDistance" : 25 * mm});
        }
    });
